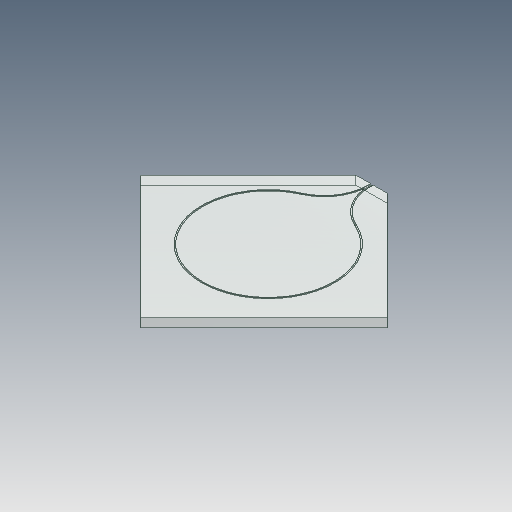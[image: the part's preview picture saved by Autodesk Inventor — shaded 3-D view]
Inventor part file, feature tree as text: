
AUTODESK INVENTOR PART (.ipt)
format: ipt  version: 2020 (Build 240168000, 168)  size: 191,488 bytes
history: native  units: mm
features: extrude x4, sketch x4, chamfer x1, fillet x1, projected_geometry x1
ambient origin geometry x8: Origin, YZ Plane, XZ Plane, XY Plane, X Axis, Y Axis, Z Axis, Center Point
bodies: Solid2 (feature_tree)
feature tree (11):
  extrude  "Extrusion12"  Depth=1.3mm
  chamfer  "Chamfer1"  Distance=200.0mm
  sketch  "Sketch13"  dims[d28=140.0mm]
  extrude  "Extrusion13"  Depth=10.0mm
  extrude  "Extrusion14"  TaperAngle=0.0deg  [1 undecoded]
  extrude  "Extrusion15"  Depth=0.65mm
  fillet  "Fillet2"  Radius=2.0mm
  sketch  "Sketch11"  dims[d5=1.3mm d19=100.0mm d20=100.0mm d21=1.3mm d22=1.3mm]
  projected_geometry  "Projected Loop11"
  sketch  "Sketch14"  dims[d80=200.0mm]
  sketch  "Sketch15"  dims[d81=45.0deg d82=200.0mm d83=10.0mm d84=0.0mm d85=25.4mm d86=2.0mm d87=45.0deg d97=1.3mm d98=1.3mm d99=1.3mm d100=100.0mm d101=100.0mm d102=150.0mm d103=3.0mm d105=90.0mm d106=3.0mm d107=1.0mm d108=11.0mm d109=145.0mm d110=0.15mm d111=17.960512mm d112=35.921024mm d113=1.15mm d114=0.0mm d115=6.15mm d116=0.0mm d117=9.0mm d118=0.0mm d119=0.65mm d120=0.5mm d121=0.872665mm d122=0.5mm d123=0.872665mm]
note: 1 required parameter value undecoded (feature->parameter linkage not recoverable at this tier; creation-order binding heuristic only, values carry confidence <= 0.55)
